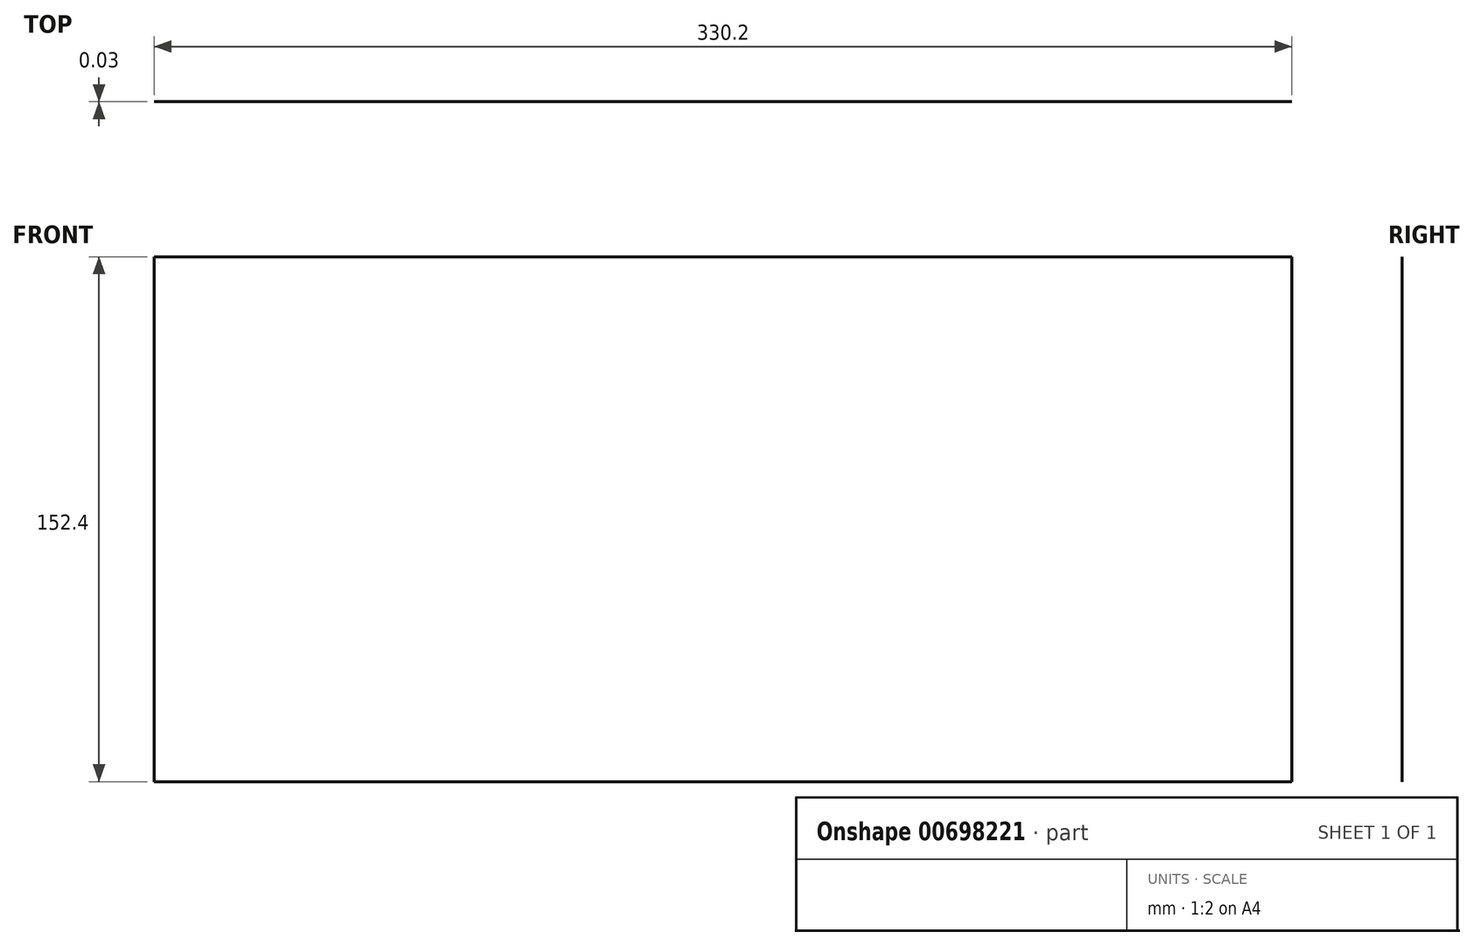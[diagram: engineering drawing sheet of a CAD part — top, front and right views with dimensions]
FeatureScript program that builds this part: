
annotation { "Feature Type Name" : "Feature", "Feature Type Description" : "" }
export const myFeature = defineFeature(function(context is Context, id is Id, definition is map)
    precondition{}
    {
        {
            var Q0;
            Q0=qCreatedBy(makeId("Front.planeOp"),FACE);
            var sketch = newSketch(context, id + "F0", { "sketchPlane" : qUnion([Q0])});
            skLineSegment(sketch, "E0.bottom", {"start": v(-220.3, -34.33) * mm, "end": v(160.7, -34.33) * mm});
            skLineSegment(sketch, "E0.top", {"start": v(-220.3, -186.73) * mm, "end": v(160.7, -186.73) * mm});
            skLineSegment(sketch, "E0.left", {"start": v(-220.3, -34.33) * mm, "end": v(-220.3, -186.73) * mm});
            skLineSegment(sketch, "E0.right", {"start": v(160.7, -34.33) * mm, "end": v(160.7, -186.73) * mm});
            skSolve(sketch);
        }
        {
            var Q0;
            Q0=makeQuery(id+"F0.imprint","IMPRINT",FACE,{"disambiguationData":[TD([[makeQuery(id+"F0.imprint","IMPRINT",EDGE,{"derivedFrom":sQuery(id+"F0.wireOp",EDGE,"E0.bottom")}),-1.0]])]});
            extrude(context, id + "F1", {"entities" : qUnion([Q0]), "depth" : 25.4 * mm, "offsetDistance" : 25.4 * mm});
        }
        {
            var Q0;
            Q0=makeQuery(id+"F1.opExtrude","SWEPT_BODY",BODY,{"disambiguationData":[OSD([sQuery(id+"F0.wireOp",EDGE,"E0.bottom"),sQuery(id+"F0.wireOp",EDGE,"E0.top"),sQuery(id+"F0.wireOp",EDGE,"E0.left"),sQuery(id+"F0.wireOp",EDGE,"E0.right")])]});
            deleteBodies(context, id + "F2", {"entities" : qUnion([Q0])});
        }
        {
            var Q0;
            Q0=qCreatedBy(makeId("Front.planeOp"),FACE);
            var sketch = newSketch(context, id + "F3", { "sketchPlane" : qUnion([Q0])});
            skLineSegment(sketch, "E1.bottom", {"start": v(-246.73, 16.83) * mm, "end": v(83.47, 16.83) * mm});
            skLineSegment(sketch, "E1.top", {"start": v(-246.73, -135.57) * mm, "end": v(83.47, -135.57) * mm});
            skLineSegment(sketch, "E1.left", {"start": v(-246.73, 16.83) * mm, "end": v(-246.73, -135.57) * mm});
            skLineSegment(sketch, "E1.right", {"start": v(83.47, 16.83) * mm, "end": v(83.47, -135.57) * mm});
            skSolve(sketch);
        }
        {
            var Q0;
            Q0=makeQuery(id+"F3.imprint","IMPRINT",FACE,{"disambiguationData":[TD([[makeQuery(id+"F3.imprint","IMPRINT",EDGE,{"derivedFrom":sQuery(id+"F3.wireOp",EDGE,"E1.bottom")}),-1.0]])]});
            extrude(context, id + "F4", {"entities" : qUnion([Q0]), "depth" : 3 / 101.6 * mm, "offsetDistance" : 25.4 * mm});
        }
    });
